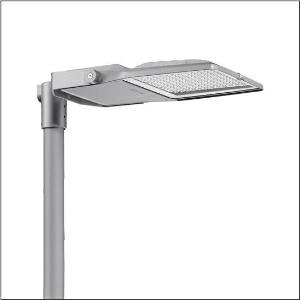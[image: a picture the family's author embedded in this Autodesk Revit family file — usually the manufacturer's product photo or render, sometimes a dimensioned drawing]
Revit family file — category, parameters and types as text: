
# Revit family: floodlight_fl_21_iq_midi___pl52_5xa7782e2d3a_7997
name_source: partatom
category: Lighting Fixtures
units: mm (PartAtom-declared; Revit-internal decimal feet)

## family parameters
Cut with Voids When Loaded = No
Host = Face
Light Source = No
Part Type = Normal
Room Calculation Point = No
Round Connector Dimension = Use Diameter
Shared = No

## types (1)
- --- (1 x LED, 26850 lm, 208.1 W, 3000K)
    Apparent Load = 208 VA
    CIE Flux Codes = 26 60 98 100 100
    Color Rendering = 70
    Color Temperature = 3000K
    Default Elevation = 1800 mm
    Description = Floodlight FL 21 iQ midi, floodlight, primary light control with lens, of PMMA, primary optical cover: protective disc, of toughened safety glass, transparent, light distribution: PL52, light emission: direct distribution, installation type: surface-mounted, LED, High Power LED, rated luminous flux: 26.850lm, luminous efficacy: 129lm/W, light colour: 730, colour temperature: 3000K, control gear: ECG iQ, control: optimised constant luminous flux control (CLO 2.0), Desk-Remote (wireless, voltage-free reading and setting of iQ features in the workshop via application-optimized NFC function/RFID function), Smart-Wire, Night-Set, Temp-Guard, Auto-Match, Street-Remote, with terminal, 6-pole, mains connection: 220..240V, AC, 50/60Hz, start of lifetime: 208W, end of service life: 227W, reduction: 90W, luminaire housing, of diecast aluminium, powder-coated, Siteco® metallic grey (DB 702S), corrosivity category C5 mid according to DIN EN ISO 12944, sealing non-destructively replaceable, please order mast flange separately, mast bracket, of steel, galvanised, powder-coated, Siteco® metallic grey (DB 702S), protection rating (complete): IP66, insulation class (complete): insulation class II (safety insulation), certification: CE, protection symbol: D, impact resistance: IK08, permissible operating ambient temperature: -40..+40°C, permissible operating ambient temperature for outdoor applications: -40..+50°C, standard: DIN EN 12944, LABS conformity tested according to VDMA 24364:2018-05, packaging unit: 1 piece

Light Distribution: PL52
    Height = 76 mm
    Lamp = 1 x LED
    Lamp Light Flux = 26850 lm
    Lamp Power = 208.1 W
    Lamp count = 1
    Length = 657 mm
    Luminous efficacy = 129 lm/W
    Manufacturer = Siteco
    ModVariant = No
    Model = 5XA7782E2D3A
    Number of Poles = 1
    OnlyDefault = Yes
    Power Factor = 1
    Product Name = Floodlight FL 21 iQ midi | PL52
    Product group = floodlight | pylon annexe
    ProductGroupID = 6200
    Protection Class = Protection class II
    Protection Degree = IP 66
    RLX_Detail_Level = 1
    RLX_Emergency_Light_Flux = 0 lm
    RLX_Emergency_Type = 0
    RLX_Emergency_Type_DB = No
    RlxData = <blob elided: 153949 chars, md5=f819a179>
    Socket = socket
    Standby Power = 0 W
    System Light Flux = 26850 lm
    System Power = 208 W
    Type Comments = factory setting: luminous flux: 100 % | dim-lin: 254 | 710 mA
    Type Image = l_1007123.jpg
    URL = http://relux.com
    VarID = @adj_036213
    Voltage = 0 V
    Weight = 0.00 kg
    Width = 442 mm

## geometry (parser evidence)
native form markers: Blend x4, Sweep x14
no freeform markers — native parametric forms only
